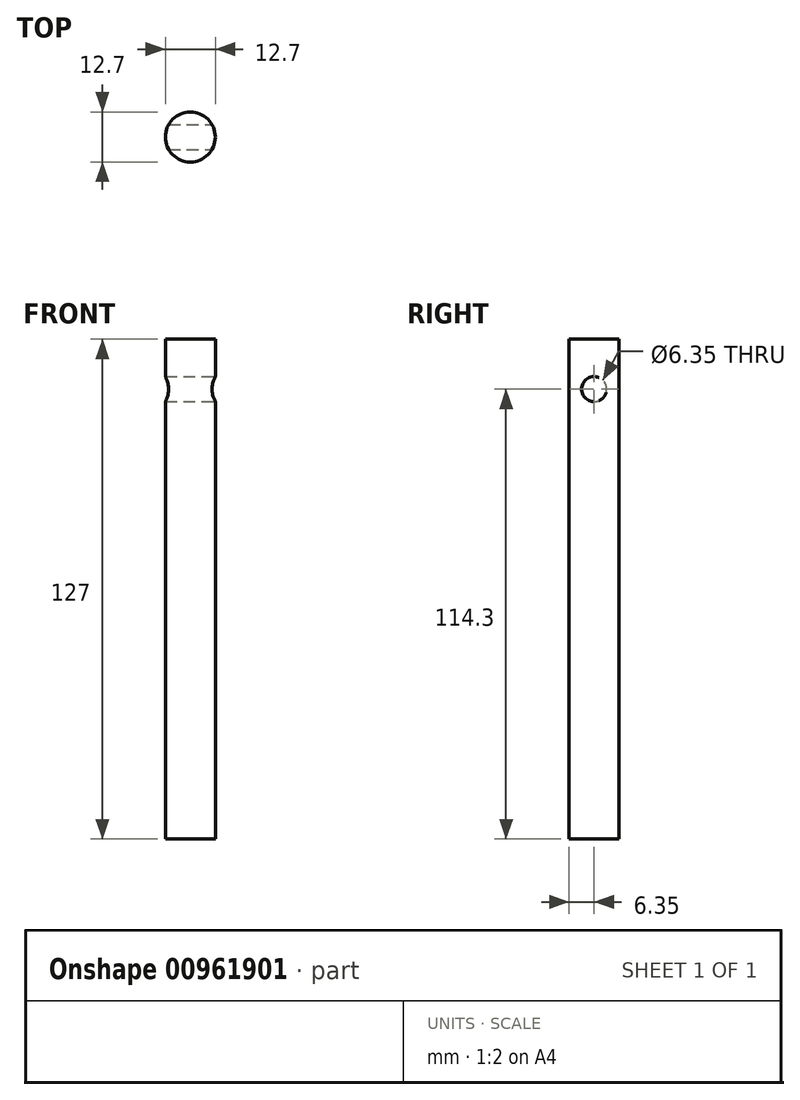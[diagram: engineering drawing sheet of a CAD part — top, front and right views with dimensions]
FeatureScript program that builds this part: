
annotation { "Feature Type Name" : "Feature", "Feature Type Description" : "" }
export const myFeature = defineFeature(function(context is Context, id is Id, definition is map)
    precondition{}
    {
        {
            var Q0;
            Q0=qCreatedBy(makeId("Top.planeOp"),FACE);
            var sketch = newSketch(context, id + "F0", { "sketchPlane" : qUnion([Q0])});
            skCircle(sketch, "E0", {"center": v(0, 0) * mm, "radius": 6.35 * mm});
            skSolve(sketch);
        }
        {
            var Q0;
            Q0 = qSketchRegion(id + "F0", true);
            extrude(context, id + "F1", {"entities" : qUnion([Q0]), "depth" : 127 * mm, "offsetDistance" : 25.4 * mm});
        }
        {
            var Q0;
            Q0=qCreatedBy(makeId("Right.planeOp"),FACE);
            var sketch = newSketch(context, id + "F2", { "sketchPlane" : qUnion([Q0])});
            skCircle(sketch, "E1", {"center": v(0, 114.3) * mm, "radius": 3.18 * mm});
            skSolve(sketch);
        }
        {
            var Q0;
            Q0 = qSketchRegion(id + "F2", true);
            extrude(context, id + "F3", {"entities" : qUnion([Q0]), "operationType" : NewBodyOperationType.REMOVE, "endBound" : BoundingType.SYMMETRIC, "oppositeDirection" : true, "depth" : 25.4 * mm, "offsetDistance" : 25.4 * mm});
        }
    });
